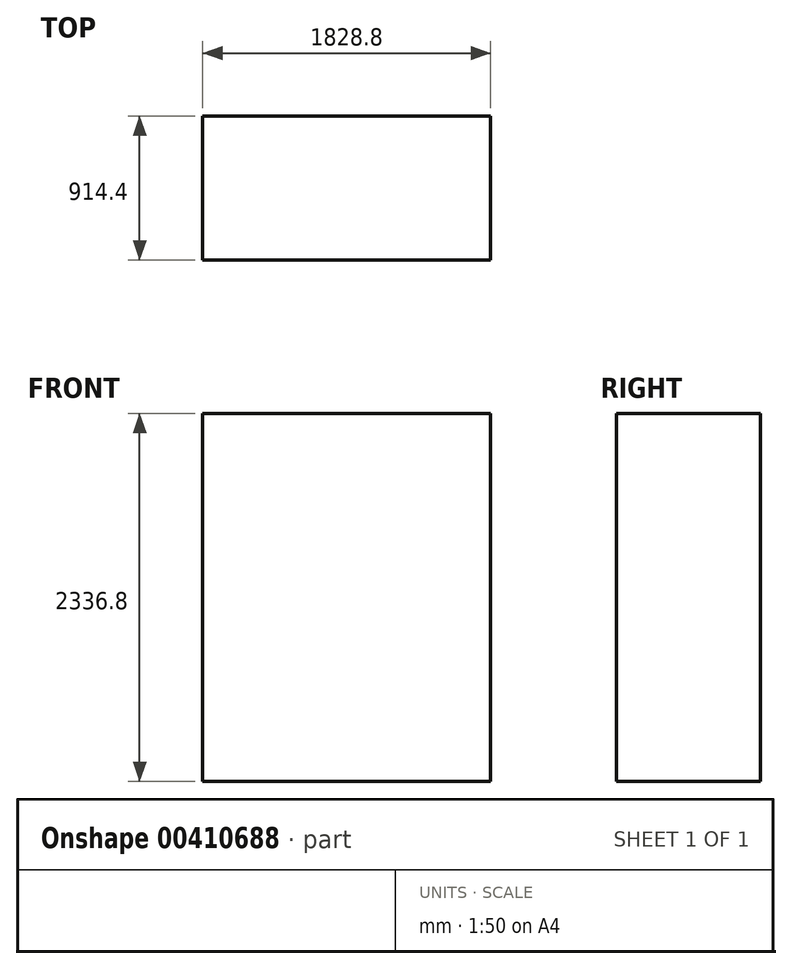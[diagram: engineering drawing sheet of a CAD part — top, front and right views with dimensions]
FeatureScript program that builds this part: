
annotation { "Feature Type Name" : "Feature", "Feature Type Description" : "" }
export const myFeature = defineFeature(function(context is Context, id is Id, definition is map)
    precondition{}
    {
        {
            var Q0;
            Q0=qCreatedBy(makeId("Front.planeOp"),FACE);
            var sketch = newSketch(context, id + "F0", { "sketchPlane" : qUnion([Q0])});
            skLineSegment(sketch, "E0", {"start": v(0, 1447.46) * mm, "end": v(0, 0) * mm, "construction": true});
            skLineSegment(sketch, "E1", {"start": v(0, 0) * mm, "end": v(-914.4, 0) * mm});
            skLineSegment(sketch, "E2", {"start": v(-914.4, 0) * mm, "end": v(-914.4, 2336.8) * mm});
            skLineSegment(sketch, "E3", {"start": v(-914.4, 2336.8) * mm, "end": v(914.4, 2336.8) * mm});
            skLineSegment(sketch, "E4", {"start": v(914.4, 2336.8) * mm, "end": v(914.4, 0) * mm});
            skLineSegment(sketch, "E5", {"start": v(914.4, 0) * mm, "end": v(0, 0) * mm});
            skSolve(sketch);
        }
        {
            var Q0;
            Q0=makeQuery(id+"F0.imprint","IMPRINT",FACE,{"disambiguationData":[TD([[makeQuery(id+"F0.imprint","IMPRINT",EDGE,{"derivedFrom":sQuery(id+"F0.wireOp",EDGE,"E1")}),-1.0]])]});
            extrude(context, id + "F1", {"entities" : qUnion([Q0]), "depth" : 914.4 * mm});
        }
    });
